# Revit family: PROOX Spare roll holder for 3 rolls EN
name_source: partatom
category: Furniture
revit_build: Autodesk Revit 2014 (Build: 20130308_1515(x64)
units: mm (PartAtom-declared; Revit-internal decimal feet)

## types (2) — shared parameters
BIM objects producer = www.BIMtelligent.eu
Manufacturer = PROOX Ltd.
Product data sheet = http://www.proox.com
URL = http://www.proox.com

## per-type parameters (varying)
| type | Cost | Description | EAN-Nummer | Material | Model | Specification |
| ONE pure | 92 $ | spare roll holder for 3 rolls PROOX ONE pure made from stainless steel | 9120050350908 | PROOX Stainless steel, brushed | PU-393 | Spare roll holder for 3 rolls made out of stainless steel. Intended for wall mounting. Surface with fine brushed structure. Cover 1.5mm thickness. |
| ONE dark passion | 99 $ | spare roll holder for 3 rolls PROOX ONE dark passion made from aluminum black anodized | 9120050350977 | PROOX Aluminum, black anodised | DP-393 | Spare roll holder for 3 rolls made out from glass pearl blasted and black anodised aluminum. For wall mounting. Surface with fine brushed strucure. Cover 3mm thickness. |

note: column(s) folded — value = type name in every type: Type Comments

## geometry (parser evidence)
native form markers: Sweep x1
no freeform markers — native parametric forms only
